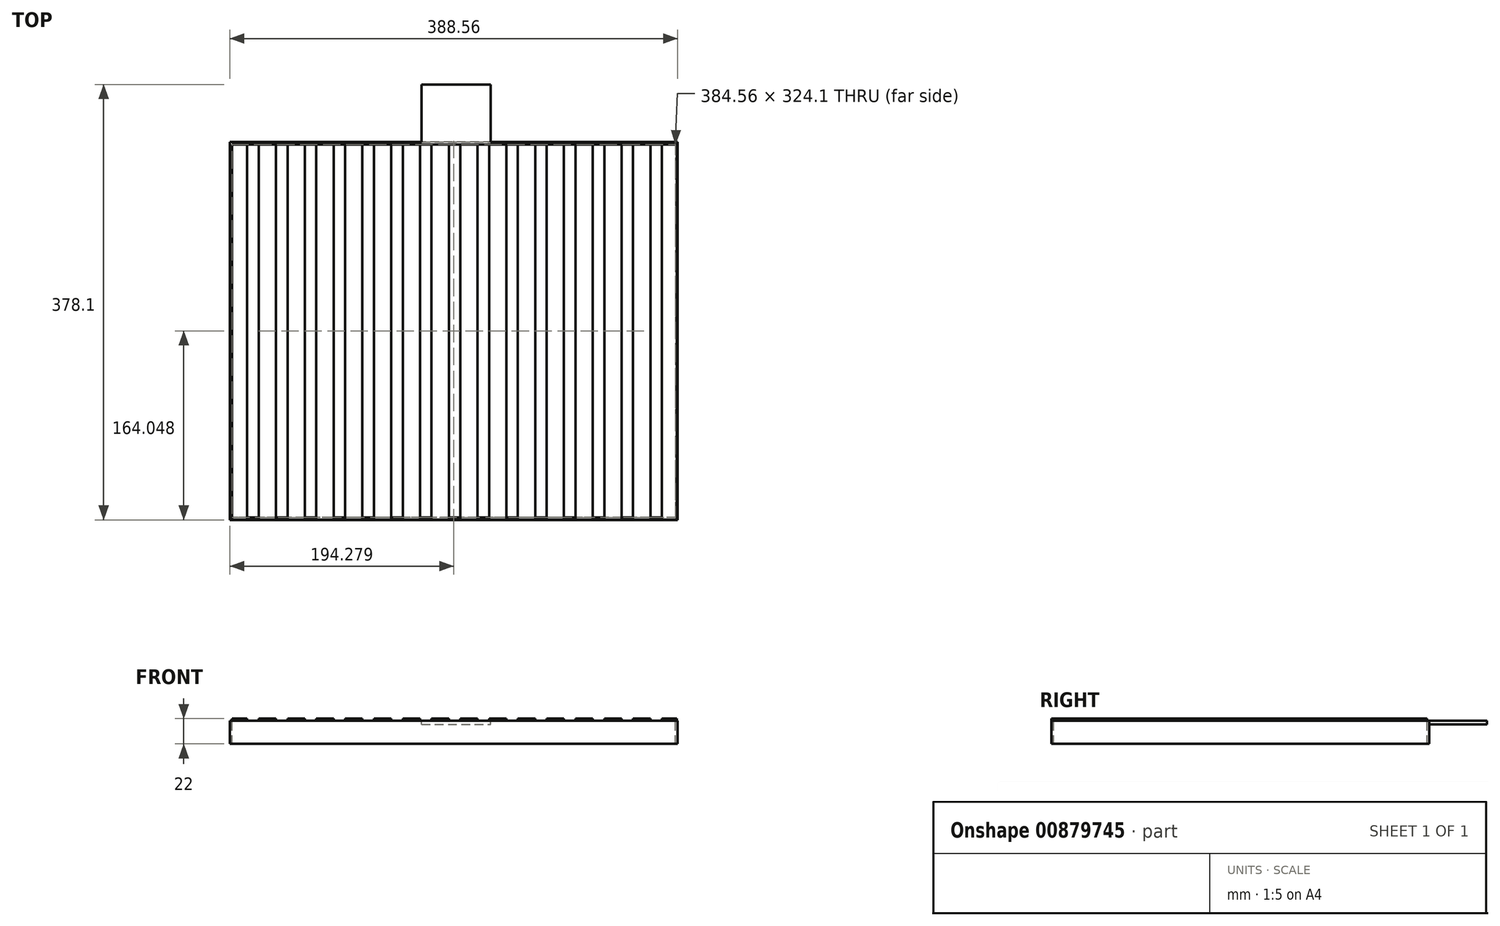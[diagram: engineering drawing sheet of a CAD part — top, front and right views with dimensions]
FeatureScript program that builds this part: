
annotation { "Feature Type Name" : "Feature", "Feature Type Description" : "" }
export const myFeature = defineFeature(function(context is Context, id is Id, definition is map)
    precondition{}
    {
        {
            var Q0;
            Q0=qCreatedBy(makeId("Top.planeOp"),FACE);
            var sketch = newSketch(context, id + "F0", { "sketchPlane" : qUnion([Q0])});
            skLineSegment(sketch, "E0.bottom", {"start": v(0, 0) * mm, "end": v(15, 0) * mm});
            skLineSegment(sketch, "E0.top", {"start": v(0, -330) * mm, "end": v(15, -330) * mm});
            skLineSegment(sketch, "E0.left", {"start": v(0, 0) * mm, "end": v(0, -330) * mm});
            skLineSegment(sketch, "E0.right", {"start": v(15, 0) * mm, "end": v(15, -330) * mm});
            skLineSegment(sketch, "E1.1.0.0", {"start": v(40, 0) * mm, "end": v(40, -330) * mm});
            skLineSegment(sketch, "E1.1.0.1", {"start": v(25, 0) * mm, "end": v(25, -330) * mm});
            skLineSegment(sketch, "E1.1.0.2", {"start": v(25, 0) * mm, "end": v(40, 0) * mm});
            skLineSegment(sketch, "E1.1.0.3", {"start": v(25, -330) * mm, "end": v(40, -330) * mm});
            skLineSegment(sketch, "E1.2.0.0", {"start": v(65, 0) * mm, "end": v(65, -330) * mm});
            skLineSegment(sketch, "E1.2.0.1", {"start": v(50, 0) * mm, "end": v(50, -330) * mm});
            skLineSegment(sketch, "E1.2.0.2", {"start": v(50, 0) * mm, "end": v(65, 0) * mm});
            skLineSegment(sketch, "E1.2.0.3", {"start": v(50, -330) * mm, "end": v(65, -330) * mm});
            skLineSegment(sketch, "E1.3.0.0", {"start": v(90, 0) * mm, "end": v(90, -330) * mm});
            skLineSegment(sketch, "E1.3.0.1", {"start": v(75, 0) * mm, "end": v(75, -330) * mm});
            skLineSegment(sketch, "E1.3.0.2", {"start": v(75, 0) * mm, "end": v(90, 0) * mm});
            skLineSegment(sketch, "E1.3.0.3", {"start": v(75, -330) * mm, "end": v(90, -330) * mm});
            skLineSegment(sketch, "E1.4.0.0", {"start": v(115, 0) * mm, "end": v(115, -330) * mm});
            skLineSegment(sketch, "E1.4.0.1", {"start": v(100, 0) * mm, "end": v(100, -330) * mm});
            skLineSegment(sketch, "E1.4.0.2", {"start": v(100, 0) * mm, "end": v(115, 0) * mm});
            skLineSegment(sketch, "E1.4.0.3", {"start": v(100, -330) * mm, "end": v(115, -330) * mm});
            skLineSegment(sketch, "E1.5.0.0", {"start": v(140, 0) * mm, "end": v(140, -330) * mm});
            skLineSegment(sketch, "E1.5.0.1", {"start": v(125, 0) * mm, "end": v(125, -330) * mm});
            skLineSegment(sketch, "E1.5.0.2", {"start": v(125, 0) * mm, "end": v(140, 0) * mm});
            skLineSegment(sketch, "E1.5.0.3", {"start": v(125, -330) * mm, "end": v(140, -330) * mm});
            skLineSegment(sketch, "E1.6.0.0", {"start": v(165, 0) * mm, "end": v(165, -330) * mm});
            skLineSegment(sketch, "E1.6.0.1", {"start": v(150, 0) * mm, "end": v(150, -330) * mm});
            skLineSegment(sketch, "E1.6.0.2", {"start": v(150, 0) * mm, "end": v(165, 0) * mm});
            skLineSegment(sketch, "E1.6.0.3", {"start": v(150, -330) * mm, "end": v(165, -330) * mm});
            skLineSegment(sketch, "E1.7.0.0", {"start": v(190, 0) * mm, "end": v(190, -330) * mm});
            skLineSegment(sketch, "E1.7.0.1", {"start": v(175, 0) * mm, "end": v(175, -330) * mm});
            skLineSegment(sketch, "E1.7.0.2", {"start": v(175, 0) * mm, "end": v(190, 0) * mm});
            skLineSegment(sketch, "E1.7.0.3", {"start": v(175, -330) * mm, "end": v(190, -330) * mm});
            skLineSegment(sketch, "E1.8.0.0", {"start": v(215, 0) * mm, "end": v(215, -330) * mm});
            skLineSegment(sketch, "E1.8.0.1", {"start": v(200, 0) * mm, "end": v(200, -330) * mm});
            skLineSegment(sketch, "E1.8.0.2", {"start": v(200, 0) * mm, "end": v(215, 0) * mm});
            skLineSegment(sketch, "E1.8.0.3", {"start": v(200, -330) * mm, "end": v(215, -330) * mm});
            skLineSegment(sketch, "E1.9.0.0", {"start": v(240, 0) * mm, "end": v(240, -330) * mm});
            skLineSegment(sketch, "E1.9.0.1", {"start": v(225, 0) * mm, "end": v(225, -330) * mm});
            skLineSegment(sketch, "E1.9.0.2", {"start": v(225, 0) * mm, "end": v(240, 0) * mm});
            skLineSegment(sketch, "E1.9.0.3", {"start": v(225, -330) * mm, "end": v(240, -330) * mm});
            skLineSegment(sketch, "E1.10.0.0", {"start": v(265, 0) * mm, "end": v(265, -330) * mm});
            skLineSegment(sketch, "E1.10.0.1", {"start": v(250, 0) * mm, "end": v(250, -330) * mm});
            skLineSegment(sketch, "E1.10.0.2", {"start": v(250, 0) * mm, "end": v(265, 0) * mm});
            skLineSegment(sketch, "E1.10.0.3", {"start": v(250, -330) * mm, "end": v(265, -330) * mm});
            skLineSegment(sketch, "E1.11.0.0", {"start": v(290, 0) * mm, "end": v(290, -330) * mm});
            skLineSegment(sketch, "E1.11.0.1", {"start": v(275, 0) * mm, "end": v(275, -330) * mm});
            skLineSegment(sketch, "E1.11.0.2", {"start": v(275, 0) * mm, "end": v(290, 0) * mm});
            skLineSegment(sketch, "E1.11.0.3", {"start": v(275, -330) * mm, "end": v(290, -330) * mm});
            skLineSegment(sketch, "E1.12.0.0", {"start": v(315, 0) * mm, "end": v(315, -330) * mm});
            skLineSegment(sketch, "E1.12.0.1", {"start": v(300, 0) * mm, "end": v(300, -330) * mm});
            skLineSegment(sketch, "E1.12.0.2", {"start": v(300, 0) * mm, "end": v(315, 0) * mm});
            skLineSegment(sketch, "E1.12.0.3", {"start": v(300, -330) * mm, "end": v(315, -330) * mm});
            skLineSegment(sketch, "E1.direction1", {"start": v(0, -330) * mm, "end": v(25, -330) * mm, "construction": true});
            skLineSegment(sketch, "E2.0.13.0", {"start": v(340, 0) * mm, "end": v(340, -330) * mm});
            skLineSegment(sketch, "E2.3.13.0", {"start": v(325, 0) * mm, "end": v(325, -330) * mm});
            skLineSegment(sketch, "E2.6.13.0", {"start": v(325, 0) * mm, "end": v(340, 0) * mm});
            skLineSegment(sketch, "E2.9.13.0", {"start": v(325, -330) * mm, "end": v(340, -330) * mm});
            skLineSegment(sketch, "E2.0.14.0", {"start": v(365, 0) * mm, "end": v(365, -330) * mm});
            skLineSegment(sketch, "E2.3.14.0", {"start": v(350, 0) * mm, "end": v(350, -330) * mm});
            skLineSegment(sketch, "E2.6.14.0", {"start": v(350, 0) * mm, "end": v(365, 0) * mm});
            skLineSegment(sketch, "E2.9.14.0", {"start": v(350, -330) * mm, "end": v(365, -330) * mm});
            skLineSegment(sketch, "E2.0.15.0", {"start": v(390, 0) * mm, "end": v(390, -330) * mm});
            skLineSegment(sketch, "E2.3.15.0", {"start": v(375, 0) * mm, "end": v(375, -330) * mm});
            skLineSegment(sketch, "E2.6.15.0", {"start": v(375, 0) * mm, "end": v(390, 0) * mm});
            skLineSegment(sketch, "E2.9.15.0", {"start": v(375, -330) * mm, "end": v(390, -330) * mm});
            skLineSegment(sketch, "E3.bottom", {"start": v(0, 0) * mm, "end": v(390, 0) * mm});
            skLineSegment(sketch, "E3.top", {"start": v(0, -330) * mm, "end": v(390, -330) * mm});
            skLineSegment(sketch, "E4.0", {"start": v(2, -328) * mm, "end": v(388, -328) * mm});
            skLineSegment(sketch, "E4.1", {"start": v(2, -2) * mm, "end": v(2, -328) * mm});
            skLineSegment(sketch, "E4.2", {"start": v(2, -2) * mm, "end": v(388, -2) * mm});
            skLineSegment(sketch, "E4.3", {"start": v(388, -2) * mm, "end": v(388, -328) * mm});
            skSolve(sketch);
        }
        {
            var Q0;
            {var subQ5=sQuery(id+"F0.wireOp",EDGE,"E4.1");Q0=makeQuery(id+"F0.imprint","IMPRINT",FACE,{"disambiguationData":[TD([[makeQuery(id+"F0.imprint","IMPRINT",EDGE,{"derivedFrom":subQ5}),1.0]])]});}
            var Q1;
            {var subQ0=sQuery(id+"F0.wireOp",EDGE,"E4.2");var subQ1=sQuery(id+"F0.wireOp",EDGE,"E1.1.0.0");var subQ2=makeQuery(id+"F0.imprint","INTERSECT",VERTEX,{"derivedFrom":[subQ1,subQ0]});Q1=makeQuery(id+"F0.imprint","IMPRINT",FACE,{"disambiguationData":[TD([[makeQuery(id+"F0.imprint","IMPRINT",EDGE,{"disambiguationData":[TD([[subQ2,-1.0]])],"derivedFrom":subQ1}),-1.0]])]});}
            var Q2;
            {var subQ0=sQuery(id+"F0.wireOp",EDGE,"E4.2");var subQ1=sQuery(id+"F0.wireOp",EDGE,"E1.2.0.0");var subQ2=makeQuery(id+"F0.imprint","INTERSECT",VERTEX,{"derivedFrom":[subQ1,subQ0]});Q2=makeQuery(id+"F0.imprint","IMPRINT",FACE,{"disambiguationData":[TD([[makeQuery(id+"F0.imprint","IMPRINT",EDGE,{"disambiguationData":[TD([[subQ2,-1.0]])],"derivedFrom":subQ1}),-1.0]])]});}
            var Q3;
            {var subQ0=sQuery(id+"F0.wireOp",EDGE,"E4.2");var subQ1=sQuery(id+"F0.wireOp",EDGE,"E1.3.0.0");var subQ2=makeQuery(id+"F0.imprint","INTERSECT",VERTEX,{"derivedFrom":[subQ1,subQ0]});Q3=makeQuery(id+"F0.imprint","IMPRINT",FACE,{"disambiguationData":[TD([[makeQuery(id+"F0.imprint","IMPRINT",EDGE,{"disambiguationData":[TD([[subQ2,-1.0]])],"derivedFrom":subQ1}),-1.0]])]});}
            var Q4;
            {var subQ0=sQuery(id+"F0.wireOp",EDGE,"E4.2");var subQ1=sQuery(id+"F0.wireOp",EDGE,"E1.4.0.0");var subQ2=makeQuery(id+"F0.imprint","INTERSECT",VERTEX,{"derivedFrom":[subQ1,subQ0]});Q4=makeQuery(id+"F0.imprint","IMPRINT",FACE,{"disambiguationData":[TD([[makeQuery(id+"F0.imprint","IMPRINT",EDGE,{"disambiguationData":[TD([[subQ2,-1.0]])],"derivedFrom":subQ1}),-1.0]])]});}
            var Q5;
            {var subQ0=sQuery(id+"F0.wireOp",EDGE,"E4.2");var subQ1=sQuery(id+"F0.wireOp",EDGE,"E1.5.0.0");var subQ2=makeQuery(id+"F0.imprint","INTERSECT",VERTEX,{"derivedFrom":[subQ1,subQ0]});Q5=makeQuery(id+"F0.imprint","IMPRINT",FACE,{"disambiguationData":[TD([[makeQuery(id+"F0.imprint","IMPRINT",EDGE,{"disambiguationData":[TD([[subQ2,-1.0]])],"derivedFrom":subQ1}),-1.0]])]});}
            var Q6;
            {var subQ0=sQuery(id+"F0.wireOp",EDGE,"E4.2");var subQ1=sQuery(id+"F0.wireOp",EDGE,"E1.6.0.0");var subQ2=makeQuery(id+"F0.imprint","INTERSECT",VERTEX,{"derivedFrom":[subQ1,subQ0]});Q6=makeQuery(id+"F0.imprint","IMPRINT",FACE,{"disambiguationData":[TD([[makeQuery(id+"F0.imprint","IMPRINT",EDGE,{"disambiguationData":[TD([[subQ2,-1.0]])],"derivedFrom":subQ1}),-1.0]])]});}
            var Q7;
            {var subQ0=sQuery(id+"F0.wireOp",EDGE,"E4.2");var subQ1=sQuery(id+"F0.wireOp",EDGE,"E1.7.0.0");var subQ2=makeQuery(id+"F0.imprint","INTERSECT",VERTEX,{"derivedFrom":[subQ1,subQ0]});Q7=makeQuery(id+"F0.imprint","IMPRINT",FACE,{"disambiguationData":[TD([[makeQuery(id+"F0.imprint","IMPRINT",EDGE,{"disambiguationData":[TD([[subQ2,-1.0]])],"derivedFrom":subQ1}),-1.0]])]});}
            var Q8;
            {var subQ0=sQuery(id+"F0.wireOp",EDGE,"E4.2");var subQ1=sQuery(id+"F0.wireOp",EDGE,"E1.8.0.0");var subQ2=makeQuery(id+"F0.imprint","INTERSECT",VERTEX,{"derivedFrom":[subQ1,subQ0]});Q8=makeQuery(id+"F0.imprint","IMPRINT",FACE,{"disambiguationData":[TD([[makeQuery(id+"F0.imprint","IMPRINT",EDGE,{"disambiguationData":[TD([[subQ2,-1.0]])],"derivedFrom":subQ1}),-1.0]])]});}
            var Q9;
            {var subQ0=sQuery(id+"F0.wireOp",EDGE,"E4.2");var subQ1=sQuery(id+"F0.wireOp",EDGE,"E1.9.0.0");var subQ2=makeQuery(id+"F0.imprint","INTERSECT",VERTEX,{"derivedFrom":[subQ1,subQ0]});Q9=makeQuery(id+"F0.imprint","IMPRINT",FACE,{"disambiguationData":[TD([[makeQuery(id+"F0.imprint","IMPRINT",EDGE,{"disambiguationData":[TD([[subQ2,-1.0]])],"derivedFrom":subQ1}),-1.0]])]});}
            var Q10;
            {var subQ0=sQuery(id+"F0.wireOp",EDGE,"E4.2");var subQ1=sQuery(id+"F0.wireOp",EDGE,"E1.10.0.0");var subQ2=makeQuery(id+"F0.imprint","INTERSECT",VERTEX,{"derivedFrom":[subQ1,subQ0]});Q10=makeQuery(id+"F0.imprint","IMPRINT",FACE,{"disambiguationData":[TD([[makeQuery(id+"F0.imprint","IMPRINT",EDGE,{"disambiguationData":[TD([[subQ2,-1.0]])],"derivedFrom":subQ1}),-1.0]])]});}
            var Q11;
            {var subQ0=sQuery(id+"F0.wireOp",EDGE,"E4.2");var subQ1=sQuery(id+"F0.wireOp",EDGE,"E1.11.0.0");var subQ2=makeQuery(id+"F0.imprint","INTERSECT",VERTEX,{"derivedFrom":[subQ1,subQ0]});Q11=makeQuery(id+"F0.imprint","IMPRINT",FACE,{"disambiguationData":[TD([[makeQuery(id+"F0.imprint","IMPRINT",EDGE,{"disambiguationData":[TD([[subQ2,-1.0]])],"derivedFrom":subQ1}),-1.0]])]});}
            var Q12;
            {var subQ0=sQuery(id+"F0.wireOp",EDGE,"E4.2");var subQ1=sQuery(id+"F0.wireOp",EDGE,"E1.12.0.0");var subQ2=makeQuery(id+"F0.imprint","INTERSECT",VERTEX,{"derivedFrom":[subQ1,subQ0]});Q12=makeQuery(id+"F0.imprint","IMPRINT",FACE,{"disambiguationData":[TD([[makeQuery(id+"F0.imprint","IMPRINT",EDGE,{"disambiguationData":[TD([[subQ2,-1.0]])],"derivedFrom":subQ1}),-1.0]])]});}
            var Q13;
            {var subQ0=sQuery(id+"F0.wireOp",EDGE,"E4.2");var subQ1=sQuery(id+"F0.wireOp",EDGE,"E2.0.13.0");var subQ2=makeQuery(id+"F0.imprint","INTERSECT",VERTEX,{"derivedFrom":[subQ1,subQ0]});Q13=makeQuery(id+"F0.imprint","IMPRINT",FACE,{"disambiguationData":[TD([[makeQuery(id+"F0.imprint","IMPRINT",EDGE,{"disambiguationData":[TD([[subQ2,-1.0]])],"derivedFrom":subQ1}),-1.0]])]});}
            var Q14;
            {var subQ0=sQuery(id+"F0.wireOp",EDGE,"E4.2");var subQ1=sQuery(id+"F0.wireOp",EDGE,"E2.0.14.0");var subQ2=makeQuery(id+"F0.imprint","INTERSECT",VERTEX,{"derivedFrom":[subQ1,subQ0]});Q14=makeQuery(id+"F0.imprint","IMPRINT",FACE,{"disambiguationData":[TD([[makeQuery(id+"F0.imprint","IMPRINT",EDGE,{"disambiguationData":[TD([[subQ2,-1.0]])],"derivedFrom":subQ1}),-1.0]])]});}
            var Q15;
            {var subQ5=sQuery(id+"F0.wireOp",EDGE,"E4.3");Q15=makeQuery(id+"F0.imprint","IMPRINT",FACE,{"disambiguationData":[TD([[makeQuery(id+"F0.imprint","IMPRINT",EDGE,{"derivedFrom":subQ5}),-1.0]])]});}
            extrude(context, id + "F1", {"entities" : qUnion([Q0, Q1, Q2, Q3, Q4, Q5, Q6, Q7, Q8, Q9, Q10, Q11, Q12, Q13, Q14, Q15]), "depth" : 2 * mm, "offsetDistance" : 25 * mm});
        }
        {
            var Q0;
            Q0=qCreatedBy(makeId("Top.planeOp"),FACE);
            var sketch = newSketch(context, id + "F2", { "sketchPlane" : qUnion([Q0])});
            skLineSegment(sketch, "E5.bottom", {"start": v(388.56, 0) * mm, "end": v(0, 0) * mm});
            skLineSegment(sketch, "E5.top", {"start": v(388.56, -328.1) * mm, "end": v(0, -328.1) * mm});
            skLineSegment(sketch, "E5.left", {"start": v(388.56, 0) * mm, "end": v(388.56, -328.1) * mm});
            skLineSegment(sketch, "E5.right", {"start": v(0, 0) * mm, "end": v(0, -328.1) * mm});
            skLineSegment(sketch, "E6.0", {"start": v(388.56, -2) * mm, "end": v(2, -2) * mm});
            skLineSegment(sketch, "E6.1", {"start": v(2, -2) * mm, "end": v(2, -326.1) * mm});
            skLineSegment(sketch, "E6.2", {"start": v(388.56, -326.1) * mm, "end": v(2, -326.1) * mm});
            skLineSegment(sketch, "E7.0", {"start": v(386.56, 0) * mm, "end": v(386.56, -328.1) * mm});
            skSolve(sketch);
        }
        {
            var Q0;
            Q0 = qSketchRegion(id + "F2", true);
            extrude(context, id + "F3", {"entities" : qUnion([Q0]), "oppositeDirection" : true, "depth" : 20 * mm, "offsetDistance" : 25 * mm});
        }
        {
            var Q0;
            Q0=qCreatedBy(makeId("Top.planeOp"),FACE);
            var sketch = newSketch(context, id + "F4", { "sketchPlane" : qUnion([Q0])});
            skLineSegment(sketch, "E8.bottom", {"start": v(166.4, 0) * mm, "end": v(226.4, 0) * mm});
            skLineSegment(sketch, "E8.top", {"start": v(166.4, 50) * mm, "end": v(226.4, 50) * mm});
            skLineSegment(sketch, "E8.left", {"start": v(166.4, 0) * mm, "end": v(166.4, 50) * mm});
            skLineSegment(sketch, "E8.right", {"start": v(226.4, 0) * mm, "end": v(226.4, 50) * mm});
            skSolve(sketch);
        }
        {
            var Q0;
            Q0=makeQuery(id+"F4.imprint","IMPRINT",FACE,{"disambiguationData":[TD([[makeQuery(id+"F4.imprint","IMPRINT",EDGE,{"derivedFrom":sQuery(id+"F4.wireOp",EDGE,"E8.bottom")}),1.0]])]});
            extrude(context, id + "F5", {"entities" : qUnion([Q0]), "operationType" : NewBodyOperationType.ADD, "oppositeDirection" : true, "depth" : 3 * mm, "offsetDistance" : 25 * mm});
        }
    });
